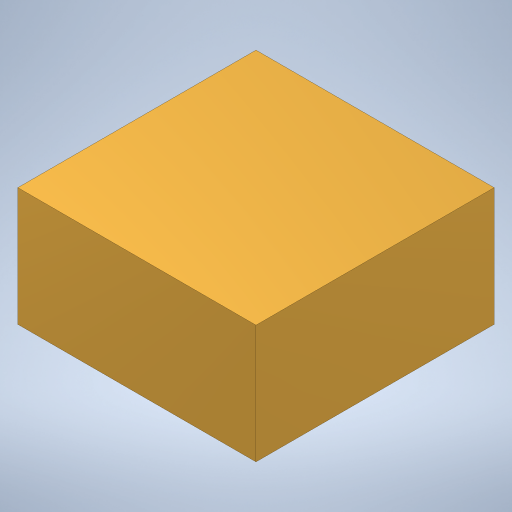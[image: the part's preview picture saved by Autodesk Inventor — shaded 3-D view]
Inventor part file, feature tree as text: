
AUTODESK INVENTOR PART (.ipt)
format: ipt  version: 2023 (Build 270158000, 158)  size: 176,640 bytes
history: native  units: in
note: dims shown in document units (in); Inventor stores cm internally (conversion verified against a paired STEP export)
features: sketch x3, extrude x1
ambient origin geometry x8: Origin, YZ Plane, XZ Plane, XY Plane, X Axis, Y Axis, Z Axis, Center Point
bodies: Solid1 (feature_tree)
feature tree (4):
  sketch  "Sketch1"  dims[d0=1.5748in d1=1.5748in]
  sketch  "Sketch2"  dims[d2=0.7829in d3=0.0in]
  extrude  "Extrusion1"  Depth=1.5748in
  sketch  "Sketch3"
